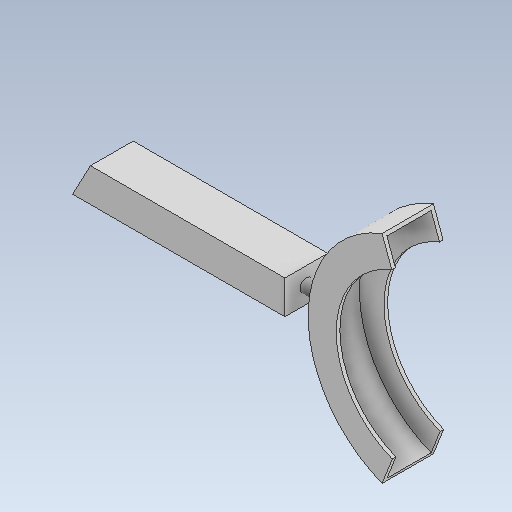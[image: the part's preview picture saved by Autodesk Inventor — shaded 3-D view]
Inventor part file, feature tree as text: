
AUTODESK INVENTOR PART (.ipt)
format: ipt  version: 2020 (Build 240168000, 168)  size: 157,696 bytes
history: native  units: mm
features: extrude x3, sketch x3, plane x1, shell x1, projected_geometry x1
ambient origin geometry x8: Origin, YZ Plane, XZ Plane, XY Plane, X Axis, Y Axis, Z Axis, Center Point
bodies: Solid1 (feature_tree)
feature tree (9):
  extrude  "Extrusion1"  Depth=26.670058mm
  extrude  "Extrusion2"  Depth=8.944mm
  plane  "Work Plane1"
  extrude  "Extrusion3"  Depth=11.775mm
  shell  "Shell1"  Thickness=0.0mm
  sketch  "Sketch2"  dims[d2=136.361055mm d3=26.670058mm]
  sketch  "Sketch3"  dims[d5=0.0mm d6=8.944mm]
  sketch  "Sketch4"  dims[d8=15.0mm d9=11.775mm d11=0.0mm d15=19.753161mm d16=3.486061mm d17=3.714968mm d18=114.810056mm d19=151.780759mm d21=0.0mm d22=2.5mm]
  projected_geometry  "Projected Loop1"
